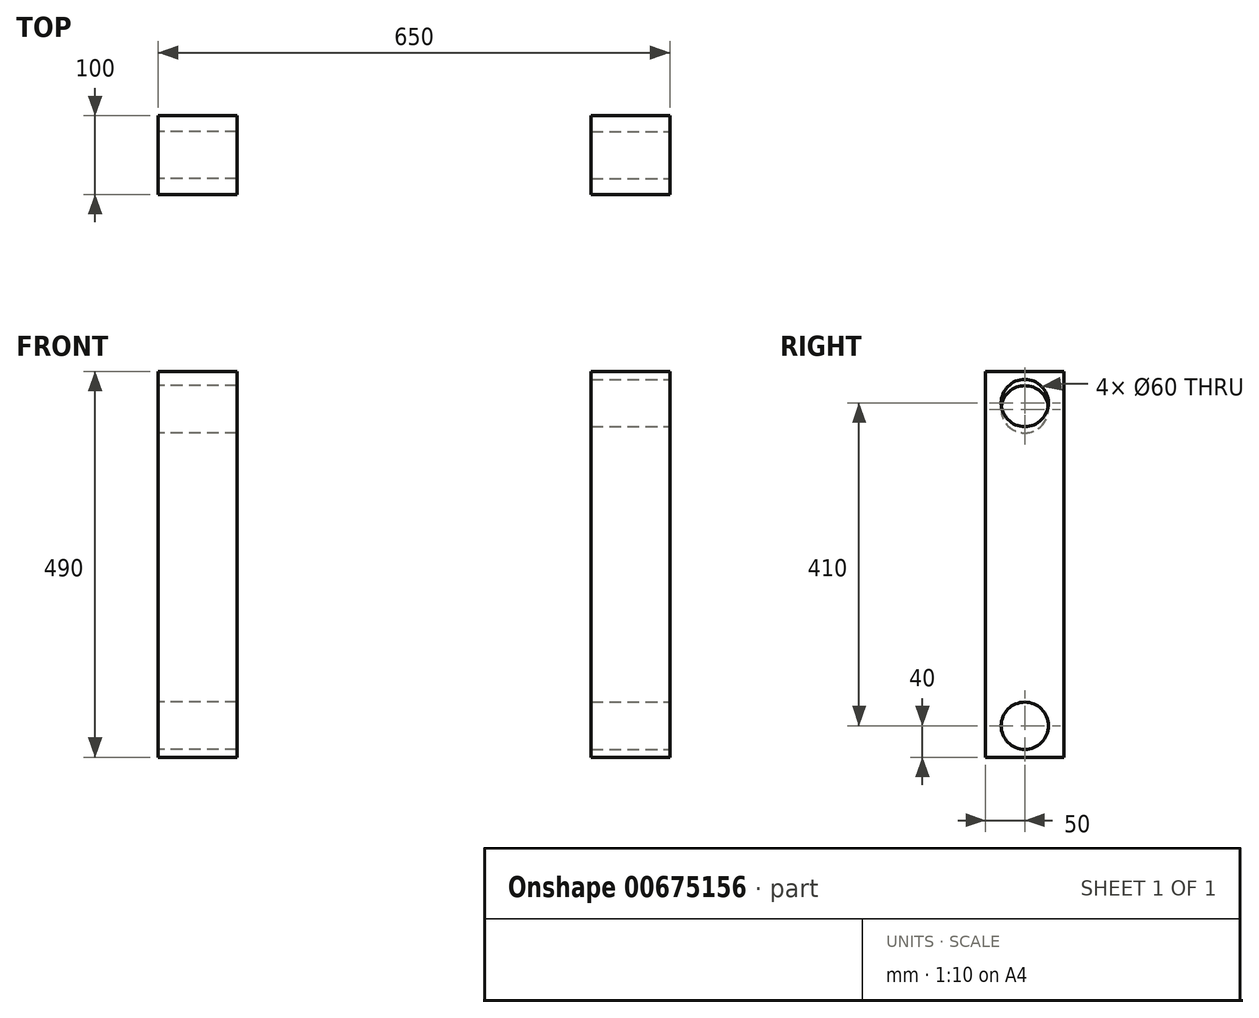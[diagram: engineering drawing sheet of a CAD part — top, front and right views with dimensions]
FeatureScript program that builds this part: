
annotation { "Feature Type Name" : "Feature", "Feature Type Description" : "" }
export const myFeature = defineFeature(function(context is Context, id is Id, definition is map)
    precondition{}
    {
        {
            var Q0;
            Q0=qCreatedBy(makeId("Top.planeOp"),FACE);
            var sketch = newSketch(context, id + "F0", { "sketchPlane" : qUnion([Q0])});
            skLineSegment(sketch, "E0.bottom", {"start": v(-325, 50) * mm, "end": v(-225, 50) * mm});
            skLineSegment(sketch, "E0.top", {"start": v(-325, -50) * mm, "end": v(-225, -50) * mm});
            skLineSegment(sketch, "E0.left", {"start": v(-325, 50) * mm, "end": v(-325, -50) * mm});
            skLineSegment(sketch, "E0.right", {"start": v(-225, 50) * mm, "end": v(-225, -50) * mm});
            skLineSegment(sketch, "E1.bottom", {"start": v(225, 50) * mm, "end": v(325, 50) * mm});
            skLineSegment(sketch, "E1.top", {"start": v(225, -50) * mm, "end": v(325, -50) * mm});
            skLineSegment(sketch, "E1.left", {"start": v(225, 50) * mm, "end": v(225, -50) * mm});
            skLineSegment(sketch, "E1.right", {"start": v(325, 50) * mm, "end": v(325, -50) * mm});
            skSolve(sketch);
        }
        {
            var Q0;
            Q0=makeQuery(id+"F0.imprint","IMPRINT",FACE,{"disambiguationData":[TD([[makeQuery(id+"F0.imprint","IMPRINT",EDGE,{"derivedFrom":sQuery(id+"F0.wireOp",EDGE,"E0.bottom")}),-1.0]])]});
            var Q1;
            Q1=makeQuery(id+"F0.imprint","IMPRINT",FACE,{"disambiguationData":[TD([[makeQuery(id+"F0.imprint","IMPRINT",EDGE,{"derivedFrom":sQuery(id+"F0.wireOp",EDGE,"E1.bottom")}),-1.0]])]});
            extrude(context, id + "F1", {"entities" : qUnion([Q0, Q1]), "depth" : 490 * mm, "offsetDistance" : 25 * mm});
        }
        {
            var Q0;
            Q0=makeQuery(id+"F1.opExtrude","SWEPT_FACE",FACE,{"disambiguationData":[OSD([sQuery(id+"F0.wireOp",EDGE,"E0.left")])]});
            var sketch = newSketch(context, id + "F2", { "sketchPlane" : qUnion([Q0])});
            skCircle(sketch, "E2", {"center": v(0, 441.98) * mm, "radius": 30 * mm});
            skSolve(sketch);
        }
        {
            var Q0;
            Q0=makeQuery(id+"F1.opExtrude","SWEPT_FACE",FACE,{"disambiguationData":[OSD([sQuery(id+"F0.wireOp",EDGE,"E1.right")])]});
            var sketch = newSketch(context, id + "F3", { "sketchPlane" : qUnion([Q0])});
            skCircle(sketch, "E3", {"center": v(0, 450) * mm, "radius": 30 * mm});
            skSolve(sketch);
        }
        {
            var Q0;
            Q0=makeQuery(id+"F2.imprint","IMPRINT",FACE,{"disambiguationData":[TD([[makeQuery(id+"F2.imprint","IMPRINT",EDGE,{"derivedFrom":sQuery(id+"F2.wireOp",EDGE,"E2")}),1.0]])]});
            extrude(context, id + "F4", {"entities" : qUnion([Q0]), "operationType" : NewBodyOperationType.REMOVE, "oppositeDirection" : true, "depth" : 100 * mm, "offsetDistance" : 25 * mm});
        }
        {
            var Q0;
            Q0=makeQuery(id+"F3.imprint","IMPRINT",FACE,{"disambiguationData":[TD([[makeQuery(id+"F3.imprint","IMPRINT",EDGE,{"derivedFrom":sQuery(id+"F3.wireOp",EDGE,"E3")}),1.0]])]});
            extrude(context, id + "F5", {"entities" : qUnion([Q0]), "operationType" : NewBodyOperationType.REMOVE, "oppositeDirection" : true, "depth" : 100 * mm, "offsetDistance" : 25 * mm});
        }
        {
            var Q0;
            Q0=makeQuery(id+"F1.opExtrude","SWEPT_FACE",FACE,{"disambiguationData":[OSD([sQuery(id+"F0.wireOp",EDGE,"E0.left")])]});
            var sketch = newSketch(context, id + "F6", { "sketchPlane" : qUnion([Q0])});
            skCircle(sketch, "E4", {"center": v(0, 40) * mm, "radius": 30 * mm});
            skSolve(sketch);
        }
        {
            var Q0;
            Q0=makeQuery(id+"F6.imprint","IMPRINT",FACE,{"disambiguationData":[TD([[makeQuery(id+"F6.imprint","IMPRINT",EDGE,{"derivedFrom":sQuery(id+"F6.wireOp",EDGE,"E4")}),1.0]])]});
            extrude(context, id + "F7", {"entities" : qUnion([Q0]), "operationType" : NewBodyOperationType.REMOVE, "oppositeDirection" : true, "depth" : 100 * mm, "offsetDistance" : 25 * mm});
        }
        {
            var Q0;
            Q0=makeQuery(id+"F1.opExtrude","SWEPT_FACE",FACE,{"disambiguationData":[OSD([sQuery(id+"F0.wireOp",EDGE,"E1.right")])]});
            var sketch = newSketch(context, id + "F8", { "sketchPlane" : qUnion([Q0])});
            skCircle(sketch, "E5", {"center": v(0, 40) * mm, "radius": 30 * mm});
            skSolve(sketch);
        }
        {
            var Q0;
            Q0=makeQuery(id+"F8.imprint","IMPRINT",FACE,{"disambiguationData":[TD([[makeQuery(id+"F8.imprint","IMPRINT",EDGE,{"derivedFrom":sQuery(id+"F8.wireOp",EDGE,"E5")}),1.0]])]});
            extrude(context, id + "F9", {"entities" : qUnion([Q0]), "operationType" : NewBodyOperationType.REMOVE, "oppositeDirection" : true, "depth" : 100 * mm, "offsetDistance" : 25 * mm});
        }
    });
